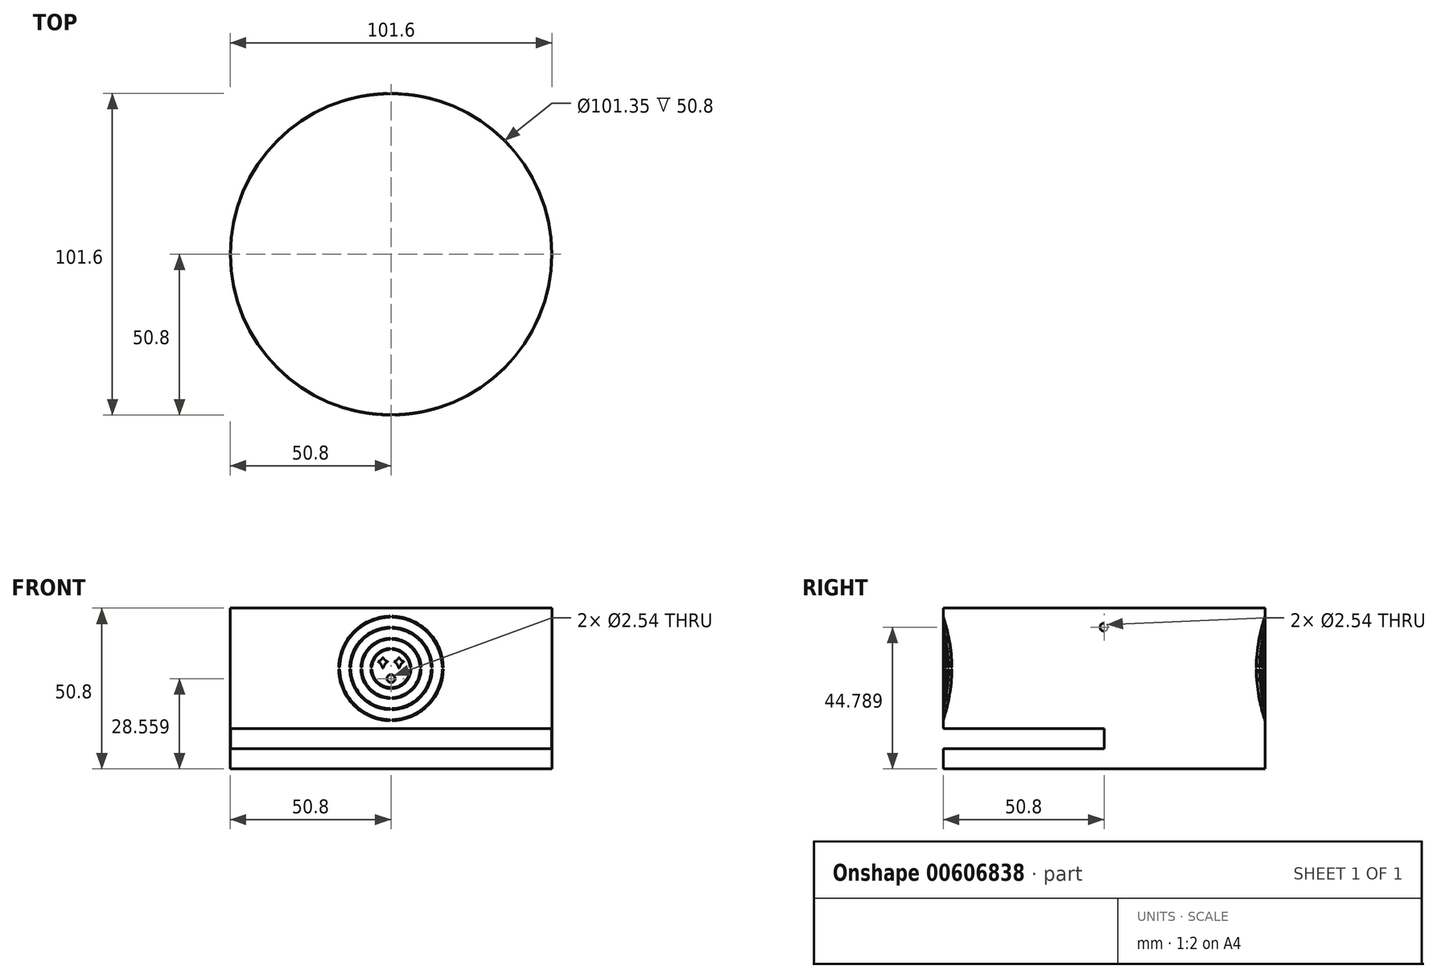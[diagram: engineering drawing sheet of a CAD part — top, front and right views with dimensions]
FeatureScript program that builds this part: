
annotation { "Feature Type Name" : "Feature", "Feature Type Description" : "" }
export const myFeature = defineFeature(function(context is Context, id is Id, definition is map)
    precondition{}
    {
        {
            var Q0;
            Q0=qCreatedBy(makeId("Front.planeOp"),FACE);
            var sketch = newSketch(context, id + "F0", { "sketchPlane" : qUnion([Q0])});
            skLineSegment(sketch, "E0.bottom", {"start": v(0, 0) * mm, "end": v(101.6, 0) * mm});
            skLineSegment(sketch, "E0.top", {"start": v(0, 50.8) * mm, "end": v(101.6, 50.8) * mm});
            skLineSegment(sketch, "E0.left", {"start": v(0, 0) * mm, "end": v(0, 50.8) * mm});
            skLineSegment(sketch, "E0.right", {"start": v(101.6, 0) * mm, "end": v(101.6, 50.8) * mm});
            skSolve(sketch);
        }
        {
            var Q0;
            Q0=makeQuery(id+"F0.imprint","IMPRINT",FACE,{"disambiguationData":[TD([[makeQuery(id+"F0.imprint","IMPRINT",EDGE,{"derivedFrom":sQuery(id+"F0.wireOp",EDGE,"E0.bottom")}),1.0]])]});
            extrude(context, id + "F1", {"entities" : qUnion([Q0]), "oppositeDirection" : true, "depth" : 101.6 * mm, "offsetDistance" : 25.4 * mm});
        }
        {
            var Q0;
            Q0=makeQuery(id+"F1.opExtrude","CAP_FACE",FACE,{"disambiguationData":[OSD([sQuery(id+"F0.wireOp",EDGE,"E0.bottom"),sQuery(id+"F0.wireOp",EDGE,"E0.top"),sQuery(id+"F0.wireOp",EDGE,"E0.left"),sQuery(id+"F0.wireOp",EDGE,"E0.right")])],"isStart":true});
            var sketch = newSketch(context, id + "F2", { "sketchPlane" : qUnion([Q0])});
            skPoint(sketch, "E1", {"position": v(0, 6.35) * mm});
            skLineSegment(sketch, "E2", {"start": v(0, 6.35) * mm, "end": v(0, 12.7) * mm});
            skLineSegment(sketch, "E3", {"start": v(0, 12.7) * mm, "end": v(101.6, 12.7) * mm});
            skLineSegment(sketch, "E4", {"start": v(0, 6.35) * mm, "end": v(101.6, 6.35) * mm});
            skLineSegment(sketch, "E5", {"start": v(101.6, 6.35) * mm, "end": v(101.6, 12.7) * mm});
            skSolve(sketch);
        }
        {
            var Q0;
            Q0=makeQuery(id+"F2.imprint","IMPRINT",FACE,{"disambiguationData":[TD([[makeQuery(id+"F2.imprint","IMPRINT",EDGE,{"derivedFrom":sQuery(id+"F2.wireOp",EDGE,"E3")}),-1.0]])]});
            extrude(context, id + "F3", {"entities" : qUnion([Q0]), "operationType" : NewBodyOperationType.REMOVE, "oppositeDirection" : true, "depth" : 50.8 * mm, "offsetDistance" : 25.4 * mm});
        }
        {
            var Q0;
            Q0=makeQuery(id+"F1.opExtrude","SWEPT_FACE",FACE,{"disambiguationData":[OSD([sQuery(id+"F0.wireOp",EDGE,"E0.right")])]});
            var sketch = newSketch(context, id + "F4", { "sketchPlane" : qUnion([Q0])});
            skPoint(sketch, "E6", {"position": v(50.8, 50.8) * mm});
            skPoint(sketch, "E7", {"position": v(50.8, 44.79) * mm});
            skCircle(sketch, "E8", {"center": v(50.8, 44.79) * mm, "radius": 1.27 * mm});
            skSolve(sketch);
        }
        {
            var Q0;
            Q0=makeQuery(id+"F4.imprint","IMPRINT",FACE,{"disambiguationData":[TD([[makeQuery(id+"F4.imprint","IMPRINT",EDGE,{"derivedFrom":sQuery(id+"F4.wireOp",EDGE,"E8")}),1.0]])]});
            extrude(context, id + "F5", {"entities" : qUnion([Q0]), "operationType" : NewBodyOperationType.REMOVE, "oppositeDirection" : true, "depth" : 127 * mm, "offsetDistance" : 25.4 * mm});
        }
        {
            var Q0;
            {var subQ0=sQuery(id+"F0.wireOp",EDGE,"E0.right");var subQ1=sQuery(id+"F0.wireOp",EDGE,"E0.top");Q0=makeQuery(id+"F3.boolean.opBoolean","SPLIT",EDGE,{"disambiguationData":[TD([makeQuery(id+"F1.opExtrude","SWEPT_FACE",FACE,{"disambiguationData":[OSD([subQ1])]})])],"derivedFrom":makeQuery(id+"F1.opExtrude","CAP_EDGE",EDGE,{"disambiguationData":[OSD([subQ0])],"isStart":true})});}
            var Q1;
            {var subQ0=sQuery(id+"F0.wireOp",EDGE,"E0.bottom");var subQ1=sQuery(id+"F0.wireOp",EDGE,"E0.right");Q1=makeQuery(id+"F3.boolean.opBoolean","SPLIT",EDGE,{"disambiguationData":[TD([makeQuery(id+"F1.opExtrude","SWEPT_FACE",FACE,{"disambiguationData":[OSD([subQ0])]})])],"derivedFrom":makeQuery(id+"F1.opExtrude","CAP_EDGE",EDGE,{"disambiguationData":[OSD([subQ1])],"isStart":true})});}
            var Q2;
            Q2=makeQuery(id+"F1.opExtrude","CAP_EDGE",EDGE,{"disambiguationData":[OSD([sQuery(id+"F0.wireOp",EDGE,"E0.right")])],"isStart":false});
            var Q3;
            {var subQ0=sQuery(id+"F0.wireOp",EDGE,"E0.left");var subQ1=sQuery(id+"F0.wireOp",EDGE,"E0.top");Q3=makeQuery(id+"F3.boolean.opBoolean","SPLIT",EDGE,{"disambiguationData":[TD([makeQuery(id+"F1.opExtrude","SWEPT_FACE",FACE,{"disambiguationData":[OSD([subQ1])]})])],"derivedFrom":makeQuery(id+"F1.opExtrude","CAP_EDGE",EDGE,{"disambiguationData":[OSD([subQ0])],"isStart":true})});}
            var Q4;
            {var subQ0=sQuery(id+"F0.wireOp",EDGE,"E0.bottom");var subQ1=sQuery(id+"F0.wireOp",EDGE,"E0.left");Q4=makeQuery(id+"F3.boolean.opBoolean","SPLIT",EDGE,{"disambiguationData":[TD([makeQuery(id+"F1.opExtrude","SWEPT_FACE",FACE,{"disambiguationData":[OSD([subQ0])]})])],"derivedFrom":makeQuery(id+"F1.opExtrude","CAP_EDGE",EDGE,{"disambiguationData":[OSD([subQ1])],"isStart":true})});}
            var Q5;
            Q5=makeQuery(id+"F1.opExtrude","CAP_EDGE",EDGE,{"disambiguationData":[OSD([sQuery(id+"F0.wireOp",EDGE,"E0.left")])],"isStart":false});
            fillet(context, id + "F6", {"entities" : qUnion([Q0, Q1, Q2, Q3, Q4, Q5]), "radius" : 50.8 * mm, "tangentPropagation" : true, "allowEdgeOverflow" : false});
        }
        {
            var Q0;
            Q0=makeQuery(id+"F1.opExtrude","SWEPT_FACE",FACE,{"disambiguationData":[OSD([sQuery(id+"F0.wireOp",EDGE,"E0.top")])]});
            var sketch = newSketch(context, id + "F7", { "sketchPlane" : qUnion([Q0])});
            skPoint(sketch, "E9", {"position": v(50.8, 50.8) * mm});
            skCircle(sketch, "E10", {"center": v(50.8, 50.8) * mm, "radius": 50.67 * mm});
            skSolve(sketch);
        }
        {
            var Q0;
            Q0=makeQuery(id+"F7.imprint","IMPRINT",FACE,{"disambiguationData":[TD([[makeQuery(id+"F7.imprint","IMPRINT",EDGE,{"derivedFrom":sQuery(id+"F7.wireOp",EDGE,"E10")}),1.0]])]});
            extrude(context, id + "F8", {"entities" : qUnion([Q0]), "operationType" : NewBodyOperationType.REMOVE, "oppositeDirection" : true, "depth" : 50.8 * mm, "offsetDistance" : 25.4 * mm});
        }
        {
            var Q0;
            Q0=qCreatedBy(makeId("Front.planeOp"),FACE);
            var sketch = newSketch(context, id + "F9", { "sketchPlane" : qUnion([Q0])});
            skLineSegment(sketch, "E11.bottom", {"start": v(0, 0) * mm, "end": v(101.6, 0) * mm});
            skLineSegment(sketch, "E11.top", {"start": v(0, 50.8) * mm, "end": v(101.6, 50.8) * mm});
            skLineSegment(sketch, "E11.left", {"start": v(0, 0) * mm, "end": v(0, 50.8) * mm});
            skLineSegment(sketch, "E11.right", {"start": v(101.6, 0) * mm, "end": v(101.6, 50.8) * mm});
            skLineSegment(sketch, "E12", {"start": v(0, 12.7) * mm, "end": v(101.6, 12.7) * mm});
            skPoint(sketch, "E13", {"position": v(50.8, 12.7) * mm});
            skPoint(sketch, "E14", {"position": v(50.8, 31.75) * mm});
            skArc(sketch, "E15", {"start": v(34.3, 31.5) * mm, "mid": v(39.13, 20.08) * mm, "end": v(50.55, 15.24) * mm});
            skArc(sketch, "E16", {"start": v(51.05, 18.73) * mm, "mid": v(60, 22.55) * mm, "end": v(63.82, 31.5) * mm});
            skArc(sketch, "E17", {"start": v(51.05, 22.23) * mm, "mid": v(57.54, 25.01) * mm, "end": v(60.32, 31.5) * mm});
            skArc(sketch, "E18", {"start": v(51.05, 25.4) * mm, "mid": v(55.3, 27.26) * mm, "end": v(57.14, 31.5) * mm});
            skPoint(sketch, "E19", {"position": v(53.34, 31.75) * mm});
            skPoint(sketch, "E20", {"position": v(48.26, 31.75) * mm});
            skLineSegment(sketch, "E21", {"start": v(53.34, 35.26) * mm, "end": v(54.08, 34.23) * mm});
            skLineSegment(sketch, "E22", {"start": v(54.08, 34.23) * mm, "end": v(54.93, 33.92) * mm});
            skLineSegment(sketch, "E23", {"start": v(54.93, 33.92) * mm, "end": v(54.08, 33.36) * mm});
            skLineSegment(sketch, "E24", {"start": v(54.08, 33.36) * mm, "end": v(53.34, 31.75) * mm});
            skLineSegment(sketch, "E25.MirrorCS", {"start": v(53.34, 35.26) * mm, "end": v(52.6, 34.23) * mm});
            skLineSegment(sketch, "E26.MirrorCS", {"start": v(52.6, 34.23) * mm, "end": v(51.75, 33.92) * mm});
            skLineSegment(sketch, "E27.MirrorCS", {"start": v(51.75, 33.92) * mm, "end": v(52.6, 33.36) * mm});
            skLineSegment(sketch, "E28.MirrorCS", {"start": v(52.6, 33.36) * mm, "end": v(53.34, 31.75) * mm});
            skLineSegment(sketch, "E29", {"start": v(48.26, 35.26) * mm, "end": v(49, 34.23) * mm});
            skLineSegment(sketch, "E30", {"start": v(49, 34.23) * mm, "end": v(49.85, 33.92) * mm});
            skLineSegment(sketch, "E31", {"start": v(49.85, 33.92) * mm, "end": v(49, 33.36) * mm});
            skLineSegment(sketch, "E32", {"start": v(49, 33.36) * mm, "end": v(48.26, 31.75) * mm});
            skLineSegment(sketch, "E33.MirrorCS", {"start": v(48.26, 35.26) * mm, "end": v(47.52, 34.23) * mm});
            skLineSegment(sketch, "E34.MirrorCS", {"start": v(47.52, 34.23) * mm, "end": v(46.67, 33.92) * mm});
            skLineSegment(sketch, "E35.MirrorCS", {"start": v(46.67, 33.92) * mm, "end": v(47.52, 33.36) * mm});
            skLineSegment(sketch, "E36.MirrorCS", {"start": v(47.52, 33.36) * mm, "end": v(48.26, 31.75) * mm});
            skPoint(sketch, "E37", {"position": v(50.8, 28.56) * mm});
            skCircle(sketch, "E38", {"center": v(50.8, 28.56) * mm, "radius": 1.27 * mm});
            skArc(sketch, "E39", {"start": v(51.05, 15.56) * mm, "mid": v(62.25, 20.3) * mm, "end": v(67, 31.5) * mm});
            skArc(sketch, "E40", {"start": v(51.05, 19.05) * mm, "mid": v(59.78, 22.77) * mm, "end": v(63.5, 31.5) * mm});
            skArc(sketch, "E41", {"start": v(51.05, 22.55) * mm, "mid": v(57.31, 25.24) * mm, "end": v(60, 31.5) * mm});
            skArc(sketch, "E42", {"start": v(51.05, 25.72) * mm, "mid": v(55.07, 27.48) * mm, "end": v(56.83, 31.5) * mm});
            skLineSegment(sketch, "E43.0", {"start": v(50.55, 31.5) * mm, "end": v(50.55, 29.8) * mm});
            skLineSegment(sketch, "E44.0", {"start": v(51.05, 31.5) * mm, "end": v(51.05, 29.8) * mm});
            skLineSegment(sketch, "E45.0", {"start": v(51.05, 31.5) * mm, "end": v(67.31, 31.5) * mm});
            skLineSegment(sketch, "E46.0", {"start": v(51.05, 32) * mm, "end": v(53.22, 32) * mm});
            skLineSegment(sketch, "E47.0", {"start": v(51.05, 32) * mm, "end": v(51.05, 48.26) * mm});
            skLineSegment(sketch, "E48.0", {"start": v(50.55, 32) * mm, "end": v(50.55, 48.26) * mm});
            skLineSegment(sketch, "E49.0", {"start": v(50.55, 32) * mm, "end": v(48.38, 32) * mm});
            skLineSegment(sketch, "E50.0", {"start": v(50.55, 31.5) * mm, "end": v(34.29, 31.5) * mm});
            skLineSegment(sketch, "E51", {"start": v(34.6, 32) * mm, "end": v(34.3, 32) * mm});
            skLineSegment(sketch, "E52.trimOffspring", {"start": v(48.14, 32) * mm, "end": v(34.6, 32) * mm});
            skLineSegment(sketch, "E53.trimOffspring", {"start": v(53.46, 32) * mm, "end": v(67.31, 32) * mm});
            skLineSegment(sketch, "E54.trimOffspring", {"start": v(51.05, 27.31) * mm, "end": v(51.05, 15.24) * mm});
            skLineSegment(sketch, "E55.trimOffspring", {"start": v(50.55, 27.31) * mm, "end": v(50.55, 15.24) * mm});
            skArc(sketch, "E56.trimOffspring", {"start": v(56.83, 32) * mm, "mid": v(55.07, 36.02) * mm, "end": v(51.05, 37.78) * mm});
            skArc(sketch, "E57.trimOffspring", {"start": v(57.14, 32) * mm, "mid": v(55.3, 36.24) * mm, "end": v(51.05, 38.1) * mm});
            skArc(sketch, "E58.trimOffspring", {"start": v(60, 32) * mm, "mid": v(57.31, 38.26) * mm, "end": v(51.05, 40.95) * mm});
            skArc(sketch, "E59.trimOffspring", {"start": v(60.32, 32) * mm, "mid": v(57.54, 38.49) * mm, "end": v(51.05, 41.27) * mm});
            skArc(sketch, "E60.trimOffspring", {"start": v(63.82, 32) * mm, "mid": v(60, 40.95) * mm, "end": v(51.05, 44.77) * mm});
            skArc(sketch, "E61.trimOffspring", {"start": v(63.5, 32) * mm, "mid": v(59.78, 40.73) * mm, "end": v(51.05, 44.45) * mm});
            skArc(sketch, "E62.trimOffspring", {"start": v(67, 32) * mm, "mid": v(62.25, 43.2) * mm, "end": v(51.05, 47.94) * mm});
            skArc(sketch, "E63.trimOffspring", {"start": v(50.55, 47.94) * mm, "mid": v(39.35, 43.2) * mm, "end": v(34.6, 32) * mm});
            skArc(sketch, "E64.trimOffspring", {"start": v(50.55, 44.77) * mm, "mid": v(41.6, 40.95) * mm, "end": v(37.78, 32) * mm});
            skArc(sketch, "E65.trimOffspring", {"start": v(50.55, 44.45) * mm, "mid": v(41.82, 40.73) * mm, "end": v(38.1, 32) * mm});
            skArc(sketch, "E66.trimOffspring", {"start": v(50.55, 41.27) * mm, "mid": v(44.06, 38.49) * mm, "end": v(41.28, 32) * mm});
            skArc(sketch, "E67.trimOffspring", {"start": v(50.55, 40.95) * mm, "mid": v(44.29, 38.26) * mm, "end": v(41.6, 32) * mm});
            skArc(sketch, "E68.trimOffspring", {"start": v(50.55, 38.1) * mm, "mid": v(46.3, 36.24) * mm, "end": v(44.46, 32) * mm});
            skArc(sketch, "E69.trimOffspring", {"start": v(50.55, 37.78) * mm, "mid": v(46.53, 36.02) * mm, "end": v(44.77, 32) * mm});
            skArc(sketch, "E70.trimOffspring", {"start": v(44.77, 31.5) * mm, "mid": v(46.53, 27.48) * mm, "end": v(50.55, 25.72) * mm});
            skArc(sketch, "E71.trimOffspring", {"start": v(44.46, 31.5) * mm, "mid": v(46.3, 27.26) * mm, "end": v(50.55, 25.4) * mm});
            skArc(sketch, "E72.trimOffspring", {"start": v(41.6, 31.5) * mm, "mid": v(44.29, 25.24) * mm, "end": v(50.55, 22.55) * mm});
            skArc(sketch, "E73.trimOffspring", {"start": v(41.28, 31.5) * mm, "mid": v(44.06, 25.01) * mm, "end": v(50.55, 22.23) * mm});
            skArc(sketch, "E74.trimOffspring", {"start": v(38.1, 31.5) * mm, "mid": v(41.82, 22.77) * mm, "end": v(50.55, 19.05) * mm});
            skArc(sketch, "E75.trimOffspring", {"start": v(37.78, 31.5) * mm, "mid": v(41.6, 22.55) * mm, "end": v(50.55, 18.73) * mm});
            skArc(sketch, "E76.trimOffspring", {"start": v(34.6, 31.5) * mm, "mid": v(39.35, 20.3) * mm, "end": v(50.55, 15.56) * mm});
            skArc(sketch, "E77.trimOffspring", {"start": v(51.05, 15.24) * mm, "mid": v(62.47, 20.08) * mm, "end": v(67.3, 31.5) * mm});
            skArc(sketch, "E78.trimOffspring", {"start": v(67.3, 32) * mm, "mid": v(62.47, 43.42) * mm, "end": v(51.05, 48.26) * mm});
            skArc(sketch, "E79.trimOffspring", {"start": v(50.55, 48.26) * mm, "mid": v(39.13, 43.42) * mm, "end": v(34.3, 32) * mm});
            skSolve(sketch);
        }
        {
            var Q0;
            {var subQ0=sQuery(id+"F9.wireOp",EDGE,"E68.trimOffspring");Q0=makeQuery(id+"F9.imprint","IMPRINT",FACE,{"disambiguationData":[TD([[makeQuery(id+"F9.imprint","IMPRINT",EDGE,{"derivedFrom":subQ0}),1.0]])]});}
            var Q1;
            Q1=makeQuery(id+"F9.imprint","IMPRINT",FACE,{"disambiguationData":[TD([[makeQuery(id+"F9.imprint","IMPRINT",EDGE,{"derivedFrom":sQuery(id+"F9.wireOp",EDGE,"E29")}),-1.0]])]});
            var Q2;
            Q2=makeQuery(id+"F9.imprint","IMPRINT",FACE,{"disambiguationData":[TD([[makeQuery(id+"F9.imprint","IMPRINT",EDGE,{"derivedFrom":sQuery(id+"F9.wireOp",EDGE,"E21")}),-1.0]])]});
            var Q3;
            {var subQ0=sQuery(id+"F9.wireOp",EDGE,"E38");var subQ1=makeQuery(id+"F9.imprint","INTERSECT",VERTEX,{"derivedFrom":[subQ0,sQuery(id+"F9.wireOp",EDGE,"E43.0")]});Q3=makeQuery(id+"F9.imprint","IMPRINT",FACE,{"disambiguationData":[TD([[makeQuery(id+"F9.imprint","IMPRINT",EDGE,{"disambiguationData":[TD([[subQ1,1.0]])],"derivedFrom":subQ0}),1.0]])]});}
            var Q4;
            {var subQ0=sQuery(id+"F9.wireOp",EDGE,"E18");Q4=makeQuery(id+"F9.imprint","IMPRINT",FACE,{"disambiguationData":[TD([[makeQuery(id+"F9.imprint","IMPRINT",EDGE,{"derivedFrom":subQ0}),1.0]])]});}
            var Q5;
            {var subQ0=sQuery(id+"F9.wireOp",EDGE,"E56.trimOffspring");Q5=makeQuery(id+"F9.imprint","IMPRINT",FACE,{"disambiguationData":[TD([[makeQuery(id+"F9.imprint","IMPRINT",EDGE,{"derivedFrom":subQ0}),-1.0]])]});}
            var Q6;
            {var subQ0=sQuery(id+"F9.wireOp",EDGE,"E70.trimOffspring");Q6=makeQuery(id+"F9.imprint","IMPRINT",FACE,{"disambiguationData":[TD([[makeQuery(id+"F9.imprint","IMPRINT",EDGE,{"derivedFrom":subQ0}),-1.0]])]});}
            var Q7;
            {var subQ0=sQuery(id+"F9.wireOp",EDGE,"E72.trimOffspring");Q7=makeQuery(id+"F9.imprint","IMPRINT",FACE,{"disambiguationData":[TD([[makeQuery(id+"F9.imprint","IMPRINT",EDGE,{"derivedFrom":subQ0}),-1.0]])]});}
            var Q8;
            {var subQ0=sQuery(id+"F9.wireOp",EDGE,"E74.trimOffspring");Q8=makeQuery(id+"F9.imprint","IMPRINT",FACE,{"disambiguationData":[TD([[makeQuery(id+"F9.imprint","IMPRINT",EDGE,{"derivedFrom":subQ0}),-1.0]])]});}
            var Q9;
            {var subQ0=sQuery(id+"F9.wireOp",EDGE,"E15");Q9=makeQuery(id+"F9.imprint","IMPRINT",FACE,{"disambiguationData":[TD([[makeQuery(id+"F9.imprint","IMPRINT",EDGE,{"derivedFrom":subQ0}),1.0]])]});}
            var Q10;
            {var subQ0=sQuery(id+"F9.wireOp",EDGE,"E39");Q10=makeQuery(id+"F9.imprint","IMPRINT",FACE,{"disambiguationData":[TD([[makeQuery(id+"F9.imprint","IMPRINT",EDGE,{"derivedFrom":subQ0}),-1.0]])]});}
            var Q11;
            {var subQ0=sQuery(id+"F9.wireOp",EDGE,"E16");Q11=makeQuery(id+"F9.imprint","IMPRINT",FACE,{"disambiguationData":[TD([[makeQuery(id+"F9.imprint","IMPRINT",EDGE,{"derivedFrom":subQ0}),1.0]])]});}
            var Q12;
            {var subQ0=sQuery(id+"F9.wireOp",EDGE,"E17");Q12=makeQuery(id+"F9.imprint","IMPRINT",FACE,{"disambiguationData":[TD([[makeQuery(id+"F9.imprint","IMPRINT",EDGE,{"derivedFrom":subQ0}),1.0]])]});}
            var Q13;
            {var subQ0=sQuery(id+"F9.wireOp",EDGE,"E58.trimOffspring");Q13=makeQuery(id+"F9.imprint","IMPRINT",FACE,{"disambiguationData":[TD([[makeQuery(id+"F9.imprint","IMPRINT",EDGE,{"derivedFrom":subQ0}),-1.0]])]});}
            var Q14;
            {var subQ0=sQuery(id+"F9.wireOp",EDGE,"E60.trimOffspring");Q14=makeQuery(id+"F9.imprint","IMPRINT",FACE,{"disambiguationData":[TD([[makeQuery(id+"F9.imprint","IMPRINT",EDGE,{"derivedFrom":subQ0}),1.0]])]});}
            var Q15;
            {var subQ0=sQuery(id+"F9.wireOp",EDGE,"E62.trimOffspring");Q15=makeQuery(id+"F9.imprint","IMPRINT",FACE,{"disambiguationData":[TD([[makeQuery(id+"F9.imprint","IMPRINT",EDGE,{"derivedFrom":subQ0}),-1.0]])]});}
            var Q16;
            Q16=makeQuery(id+"F9.imprint","IMPRINT",FACE,{"disambiguationData":[TD([[makeQuery(id+"F9.imprint","IMPRINT",EDGE,{"derivedFrom":sQuery(id+"F9.wireOp",EDGE,"E51")}),-1.0]])]});
            var Q17;
            {var subQ0=sQuery(id+"F9.wireOp",EDGE,"E64.trimOffspring");Q17=makeQuery(id+"F9.imprint","IMPRINT",FACE,{"disambiguationData":[TD([[makeQuery(id+"F9.imprint","IMPRINT",EDGE,{"derivedFrom":subQ0}),1.0]])]});}
            var Q18;
            {var subQ0=sQuery(id+"F9.wireOp",EDGE,"E66.trimOffspring");Q18=makeQuery(id+"F9.imprint","IMPRINT",FACE,{"disambiguationData":[TD([[makeQuery(id+"F9.imprint","IMPRINT",EDGE,{"derivedFrom":subQ0}),1.0]])]});}
            extrude(context, id + "F10", {"entities" : qUnion([Q0, Q1, Q2, Q3, Q4, Q5, Q6, Q7, Q8, Q9, Q10, Q11, Q12, Q13, Q14, Q15, Q16, Q17, Q18]), "operationType" : NewBodyOperationType.REMOVE, "oppositeDirection" : true, "depth" : 127 * mm, "offsetDistance" : 25.4 * mm});
        }
    });
